FCSTD DOCUMENT  (FreeCAD 0.18R14235 (Git))
Label: SPU0410LR5H
License: All rights reserved
LicenseURL: http://en.wikipedia.org/wiki/All_rights_reserved
objects: Sketcher::SketchObject×10, App::Annotation×2, Image::ImagePlane×1, App::DocumentObjectGroup×1
note: 10 computed .brp shape members not serialized (recipe doc carries the construction recipe); baked Part::Feature solids carry a one-line shape summary decoded from their .brp

FEATURE [Sketcher::SketchObject] Sketch  label="Pads_TH_SMD"
  sketch-geometry (5):
    g0: Circle CenterX=0.966 CenterY=2.103 CenterZ=0 NormalX=0 NormalY=0 NormalZ=1 AngleXU=0 Radius=0.3615
    g1: Circle CenterX=0 CenterY=2.103 CenterZ=0 NormalX=0 NormalY=0 NormalZ=1 AngleXU=0 Radius=0.31
    g2: Circle CenterX=-0.966 CenterY=2.103 CenterZ=0 NormalX=0 NormalY=0 NormalZ=1 AngleXU=0 Radius=0.3615
    g3: Circle CenterX=1.0155 CenterY=-0.634 CenterZ=0 NormalX=0 NormalY=0 NormalZ=1 AngleXU=0 Radius=0.281
    g4: Circle CenterX=-1.016 CenterY=-0.634 CenterZ=0 NormalX=0 NormalY=0 NormalZ=1 AngleXU=0 Radius=0.281
  constraints (5):
    c: Equal(g4,g3)
    c: Radius(g1) = 0.31
    c: Equal(g0,g2)
    c: Diameter(g0) = 0.723
    c: Diameter(g3) = 0.562
FEATURE [Sketcher::SketchObject] Sketch001  label="F_Silks_0.16"
  sketch-geometry (12):
    g0: ArcOfCircle [constr] CenterX=-1.5 CenterY=2.636 CenterZ=0 NormalX=0 NormalY=0 NormalZ=1 AngleXU=1.5708 Radius=0.05 StartAngle=0 EndAngle=3.14159
    g1: ArcOfCircle [constr] CenterX=1.5 CenterY=2.636 CenterZ=0 NormalX=0 NormalY=0 NormalZ=1 AngleXU=1.5708 Radius=0.05 StartAngle=3.14159 EndAngle=6.28319
    g2: ArcOfCircle [constr] CenterX=1.5 CenterY=2.636 CenterZ=0 NormalX=0 NormalY=0 NormalZ=1 AngleXU=0 Radius=0.05 StartAngle=0 EndAngle=3.14159
    g3: ArcOfCircle [constr] CenterX=1.5 CenterY=-1.124 CenterZ=0 NormalX=0 NormalY=0 NormalZ=1 AngleXU=0 Radius=0.05 StartAngle=3.14159 EndAngle=6.28319
    g4: ArcOfCircle [constr] CenterX=1.5 CenterY=-1.124 CenterZ=0 NormalX=0 NormalY=0 NormalZ=1 AngleXU=-1.5708 Radius=0.05 StartAngle=0 EndAngle=3.14159
    g5: ArcOfCircle [constr] CenterX=-1.5 CenterY=-1.124 CenterZ=0 NormalX=0 NormalY=0 NormalZ=1 AngleXU=-1.5708 Radius=0.05 StartAngle=3.14159 EndAngle=6.28319
    g6: ArcOfCircle [constr] CenterX=-1.5 CenterY=-1.124 CenterZ=0 NormalX=0 NormalY=0 NormalZ=1 AngleXU=3.14159 Radius=0.05 StartAngle=0 EndAngle=3.14159
    g7: ArcOfCircle [constr] CenterX=-1.5 CenterY=2.636 CenterZ=0 NormalX=0 NormalY=0 NormalZ=1 AngleXU=3.14159 Radius=0.05 StartAngle=3.14159 EndAngle=6.28319
    g8: LineSegment StartX=-1.5 StartY=2.636 StartZ=0 EndX=1.5 EndY=2.636 EndZ=0
    g9: LineSegment StartX=1.5 StartY=2.636 StartZ=0 EndX=1.5 EndY=-1.124 EndZ=0
    g10: LineSegment StartX=-1.5 StartY=2.636 StartZ=0 EndX=-1.5 EndY=-1.124 EndZ=0
    g11: LineSegment StartX=-1.5 StartY=-1.124 StartZ=0 EndX=1.5 EndY=-1.124 EndZ=0
  constraints (8):
    c: Coincident(g1,g8)
    c: Coincident(g0,g8)
    c: Coincident(g8,g10)
    c: Coincident(g8,g9)
    c: Coincident(g5,g10)
    c: Coincident(g5,g11)
    c: Coincident(g3,g11)
    c: Coincident(g3,g9)
FEATURE [Sketcher::SketchObject] Sketch002  label="Pads_Geom_0.31"
  sketch-geometry (2):
    g0: Circle CenterX=0 CenterY=0 CenterZ=0 NormalX=0 NormalY=0 NormalZ=1 AngleXU=0 Radius=0.4585
    g1: Circle [constr] CenterX=0 CenterY=0.4585 CenterZ=0 NormalX=0 NormalY=0 NormalZ=1 AngleXU=0 Radius=0.155
  constraints (4):
    c: Diameter(g0) = 0.917
    c: DistanceX(g0,g1) = 0
    c: DistanceY(g0,g1) = 0.4585
    c: Diameter(g1) = 0.31
FEATURE [Sketcher::SketchObject] Sketch003  label="Pads_NPTH"
  sketch-geometry (1):
    g0: Circle CenterX=0 CenterY=0 CenterZ=0 NormalX=0 NormalY=0 NormalZ=1 AngleXU=0 Radius=0.125
  constraints (1):
    c: Radius(g0) = 0.125
FEATURE [Image::ImagePlane] ImagePlane
  Placement = pos=(-0.02,0.875,-1) rot=(0,0,1;0rad)
  XSize = 7.03286
  YSize = 8.70404
FEATURE [App::Annotation] Text  label="Ref#_0.8mm"
  LabelText = REF**
  Position = (0,2.8,0)
FEATURE [App::Annotation] Text001  label="Value#_0.8mm"
  LabelText = Value 
  Position = (0,-2,0)
FEATURE [Sketcher::SketchObject] Sketch004  label="F_CrtYd_0.05"
  sketch-geometry (12):
    g0: ArcOfCircle [constr] CenterX=-1.5 CenterY=2.636 CenterZ=0 NormalX=0 NormalY=0 NormalZ=1 AngleXU=1.5708 Radius=0.05 StartAngle=0 EndAngle=3.14159
    g1: ArcOfCircle [constr] CenterX=1.5 CenterY=2.636 CenterZ=0 NormalX=0 NormalY=0 NormalZ=1 AngleXU=1.5708 Radius=0.05 StartAngle=3.14159 EndAngle=6.28319
    g2: ArcOfCircle [constr] CenterX=1.5 CenterY=2.636 CenterZ=0 NormalX=0 NormalY=0 NormalZ=1 AngleXU=0 Radius=0.05 StartAngle=0 EndAngle=3.14159
    g3: ArcOfCircle [constr] CenterX=1.5 CenterY=-1.124 CenterZ=0 NormalX=0 NormalY=0 NormalZ=1 AngleXU=0 Radius=0.05 StartAngle=3.14159 EndAngle=6.28319
    g4: ArcOfCircle [constr] CenterX=1.5 CenterY=-1.124 CenterZ=0 NormalX=0 NormalY=0 NormalZ=1 AngleXU=-1.5708 Radius=0.05 StartAngle=0 EndAngle=3.14159
    g5: ArcOfCircle [constr] CenterX=-1.5 CenterY=-1.124 CenterZ=0 NormalX=0 NormalY=0 NormalZ=1 AngleXU=-1.5708 Radius=0.05 StartAngle=3.14159 EndAngle=6.28319
    g6: ArcOfCircle [constr] CenterX=-1.5 CenterY=-1.124 CenterZ=0 NormalX=0 NormalY=0 NormalZ=1 AngleXU=-3.14159 Radius=0.05 StartAngle=0 EndAngle=3.14159
    g7: ArcOfCircle [constr] CenterX=-1.5 CenterY=2.636 CenterZ=0 NormalX=0 NormalY=0 NormalZ=1 AngleXU=-3.14159 Radius=0.05 StartAngle=3.14159 EndAngle=6.28319
    g8: LineSegment StartX=-1.5 StartY=2.636 StartZ=0 EndX=1.5 EndY=2.636 EndZ=0
    g9: LineSegment StartX=1.5 StartY=2.636 StartZ=0 EndX=1.5 EndY=-1.124 EndZ=0
    g10: LineSegment StartX=-1.5 StartY=2.636 StartZ=0 EndX=-1.5 EndY=-1.124 EndZ=0
    g11: LineSegment StartX=-1.5 StartY=-1.124 StartZ=0 EndX=1.5 EndY=-1.124 EndZ=0
  constraints (8):
    c: Coincident(g1,g8)
    c: Coincident(g0,g8)
    c: Coincident(g8,g10)
    c: Coincident(g8,g9)
    c: Coincident(g5,g10)
    c: Coincident(g5,g11)
    c: Coincident(g3,g11)
    c: Coincident(g3,g9)
FEATURE [Sketcher::SketchObject] Sketch005  label="F_Fab_0.1"
  sketch-geometry (12):
    g0: ArcOfCircle [constr] CenterX=-1.5 CenterY=2.636 CenterZ=0 NormalX=0 NormalY=0 NormalZ=1 AngleXU=1.5708 Radius=0.05 StartAngle=0 EndAngle=3.14159
    g1: ArcOfCircle [constr] CenterX=1.5 CenterY=2.636 CenterZ=0 NormalX=0 NormalY=0 NormalZ=1 AngleXU=1.5708 Radius=0.05 StartAngle=3.14159 EndAngle=6.28319
    g2: ArcOfCircle [constr] CenterX=1.5 CenterY=2.636 CenterZ=0 NormalX=0 NormalY=0 NormalZ=1 AngleXU=0 Radius=0.05 StartAngle=0 EndAngle=3.14159
    g3: ArcOfCircle [constr] CenterX=1.5 CenterY=-1.124 CenterZ=0 NormalX=0 NormalY=0 NormalZ=1 AngleXU=0 Radius=0.05 StartAngle=3.14159 EndAngle=6.28319
    g4: ArcOfCircle [constr] CenterX=1.5 CenterY=-1.124 CenterZ=0 NormalX=0 NormalY=0 NormalZ=1 AngleXU=-1.5708 Radius=0.05 StartAngle=0 EndAngle=3.14159
    g5: ArcOfCircle [constr] CenterX=-1.5 CenterY=-1.124 CenterZ=0 NormalX=0 NormalY=0 NormalZ=1 AngleXU=-1.5708 Radius=0.05 StartAngle=3.14159 EndAngle=6.28319
    g6: ArcOfCircle [constr] CenterX=-1.5 CenterY=-1.124 CenterZ=0 NormalX=0 NormalY=0 NormalZ=1 AngleXU=3.14159 Radius=0.05 StartAngle=0 EndAngle=3.14159
    g7: ArcOfCircle [constr] CenterX=-1.5 CenterY=2.636 CenterZ=0 NormalX=0 NormalY=0 NormalZ=1 AngleXU=3.14159 Radius=0.05 StartAngle=3.14159 EndAngle=6.28319
    g8: LineSegment StartX=-1.5 StartY=2.636 StartZ=0 EndX=1.5 EndY=2.636 EndZ=0
    g9: LineSegment StartX=1.5 StartY=2.636 StartZ=0 EndX=1.5 EndY=-1.124 EndZ=0
    g10: LineSegment StartX=-1.5 StartY=2.636 StartZ=0 EndX=-1.5 EndY=-1.124 EndZ=0
    g11: LineSegment StartX=-1.5 StartY=-1.124 StartZ=0 EndX=1.5 EndY=-1.124 EndZ=0
  constraints (8):
    c: Coincident(g1,g8)
    c: Coincident(g0,g8)
    c: Coincident(g8,g10)
    c: Coincident(g8,g9)
    c: Coincident(g5,g10)
    c: Coincident(g5,g11)
    c: Coincident(g3,g11)
    c: Coincident(g3,g9)
FEATURE [Sketcher::SketchObject] Sketch006  label="Pads_Poly"
  sketch-geometry (6):
    g0: LineSegment StartX=0.183302 StartY=0.243773 StartZ=0 EndX=0.401456 EndY=0.461928 EndZ=0
    g1: LineSegment [constr] StartX=0 StartY=0 StartZ=0 EndX=0.704847 EndY=0.704847 EndZ=0
    g2: ArcOfCircle CenterX=0 CenterY=0 CenterZ=0 NormalX=0 NormalY=0 NormalZ=1 AngleXU=0 Radius=0.305 StartAngle=0.926058 EndAngle=2.21514
    g3: ArcOfCircle CenterX=0 CenterY=0 CenterZ=0 NormalX=0 NormalY=0 NormalZ=1 AngleXU=0 Radius=0.612 StartAngle=0.855324 EndAngle=2.26677
    g4: Circle CenterX=0 CenterY=0.4585 CenterZ=0 NormalX=0 NormalY=0 NormalZ=1 AngleXU=0 Radius=0.07525
    g5: LineSegment StartX=-0.183303 StartY=0.243772 StartZ=0 EndX=-0.392373 EndY=0.469668 EndZ=0
  constraints (14):
    c: Angle(g-1,g1) = 0.785398
    c: Parallel(g1,g0)
    c: DistanceX(g2,g4) = 0
    c: Diameter(g2) = 0.61
    c: Coincident(g1,g3)
    c: Coincident(g1,g-1)
    c: Coincident(g2,g3)
    c: Diameter(g4) = 0.1505
    c: DistanceY(g2,g4) = 0.4585
    c: Coincident(g2,g0)
    c: Diameter(g3) = 1.224
    c: Coincident(g3,g0)
    c: Coincident(g3,g5)
    c: Distance(g0,g1) = 0.04276
FEATURE [Sketcher::SketchObject] Sketch007  label="Pads_Poly001"
  sketch-geometry (6):
    g0: LineSegment [constr] StartX=0 StartY=0 StartZ=0 EndX=0.704847 EndY=0.704847 EndZ=0
    g1: LineSegment StartX=0.183303 StartY=-0.243772 StartZ=0 EndX=0.401457 EndY=-0.461927 EndZ=0
    g2: ArcOfCircle CenterX=0 CenterY=0 CenterZ=0 NormalX=0 NormalY=0 NormalZ=1 AngleXU=0 Radius=0.305 StartAngle=4.06805 EndAngle=5.35713
    g3: ArcOfCircle CenterX=0 CenterY=0 CenterZ=0 NormalX=0 NormalY=0 NormalZ=1 AngleXU=0 Radius=0.612 StartAngle=4.01642 EndAngle=5.42786
    g4: Circle CenterX=0 CenterY=-0.4585 CenterZ=0 NormalX=0 NormalY=0 NormalZ=1 AngleXU=0 Radius=0.07525
    g5: LineSegment StartX=-0.183303 StartY=-0.243772 StartZ=0 EndX=-0.392373 EndY=-0.469668 EndZ=0
  constraints (10):
    c: Angle(g-1,g0) = 0.785398
    c: Coincident(g0,g-1)
    c: Diameter(g2) = 0.61
    c: Coincident(g2,g3)
    c: Diameter(g4) = 0.1505
    c: Coincident(g2,g1)
    c: Diameter(g3) = 1.224
    c: Coincident(g3,g1)
    c: Coincident(g3,g5)
    c: DistanceX(g4,g2) = 0
FEATURE [Sketcher::SketchObject] Sketch009  label="Pads_Poly002"
  sketch-geometry (7):
    g0: LineSegment StartX=0.243773 StartY=-0.183302 StartZ=0 EndX=0.461928 EndY=-0.401456 EndZ=0
    g1: LineSegment [constr] StartX=0 StartY=0 StartZ=0 EndX=0.926911 EndY=-0.926911 EndZ=0
    g2: ArcOfCircle CenterX=0 CenterY=0 CenterZ=0 NormalX=0 NormalY=0 NormalZ=1 AngleXU=0 Radius=0.305 StartAngle=5.63845 EndAngle=6.92792
    g3: ArcOfCircle CenterX=0 CenterY=0 CenterZ=0 NormalX=0 NormalY=0 NormalZ=1 AngleXU=0 Radius=0.612 StartAngle=5.56771 EndAngle=6.99866
    g4: Circle CenterX=0.4585 CenterY=0 CenterZ=0 NormalX=0 NormalY=0 NormalZ=1 AngleXU=0 Radius=0.07525
    g5: LineSegment StartX=0.243773 StartY=0.183302 StartZ=0 EndX=0.461928 EndY=0.401456 EndZ=0
    g6: LineSegment [constr] StartX=0 StartY=0 StartZ=0 EndX=0.885285 EndY=0.885285 EndZ=0
  constraints (19):
    c: Angle(g-1,g1) = -0.785398
    c: Parallel(g1,g0)
    c: Diameter(g2) = 0.61
    c: Coincident(g1,g3)
    c: Coincident(g1,g-1)
    c: Coincident(g2,g3)
    c: Diameter(g4) = 0.1505
    c: Coincident(g2,g0)
    c: Diameter(g3) = 1.224
    c: Coincident(g3,g0)
    c: Coincident(g3,g5)
    c: Distance(g0,g1) = 0.04276
    c: Parallel(g6,g5)
    c: Coincident(g5,g2)
    c: Coincident(g6,g2)
    c: Angle(g-1,g6) = 0.785398
    c: Distance(g2,g6) = 0.04276
    c: Distance(g4,g2) = 0.4585
    c: DistanceY(g2,g4) = 0
FEATURE [Sketcher::SketchObject] Sketch010  label="Pads_Poly003"
  sketch-geometry (7):
    g0: LineSegment StartX=-0.243773 StartY=-0.183302 StartZ=0 EndX=-0.461928 EndY=-0.401456 EndZ=0
    g1: LineSegment [constr] StartX=0 StartY=0 StartZ=0 EndX=-0.926911 EndY=-0.926911 EndZ=0
    g2: ArcOfCircle CenterX=0 CenterY=0 CenterZ=0 NormalX=0 NormalY=0 NormalZ=1 AngleXU=0 Radius=0.305 StartAngle=2.49685 EndAngle=3.78633
    g3: ArcOfCircle CenterX=0 CenterY=0 CenterZ=0 NormalX=0 NormalY=0 NormalZ=1 AngleXU=0 Radius=0.612 StartAngle=2.42612 EndAngle=3.85706
    g4: Circle CenterX=-0.4585 CenterY=0 CenterZ=0 NormalX=0 NormalY=0 NormalZ=1 AngleXU=0 Radius=0.07525
    g5: LineSegment StartX=-0.243773 StartY=0.183302 StartZ=0 EndX=-0.461928 EndY=0.401456 EndZ=0
    g6: LineSegment [constr] StartX=0 StartY=0 StartZ=0 EndX=-0.885285 EndY=0.885285 EndZ=0
  constraints (16):
    c: Parallel(g1,g0)
    c: Diameter(g2) = 0.61
    c: Coincident(g1,g3)
    c: Coincident(g2,g3)
    c: Diameter(g4) = 0.1505
    c: Coincident(g2,g0)
    c: Diameter(g3) = 1.224
    c: Coincident(g3,g0)
    c: Coincident(g3,g5)
    c: Distance(g0,g1) = 0.04276
    c: Parallel(g6,g5)
    c: Coincident(g5,g2)
    c: Coincident(g6,g2)
    c: Distance(g2,g6) = 0.04276
    c: Distance(g4,g2) = 0.4585
    c: DistanceY(g4,g2) = 0
FEATURE [App::DocumentObjectGroup] Group  label="SPU0410LR5H_fp"
  Group = -> [Text,Text001,Sketch001,Sketch004,Sketch005,Sketch,Sketch003,Sketch006,Sketch007,Sketch009,Sketch010,Sketch002]
